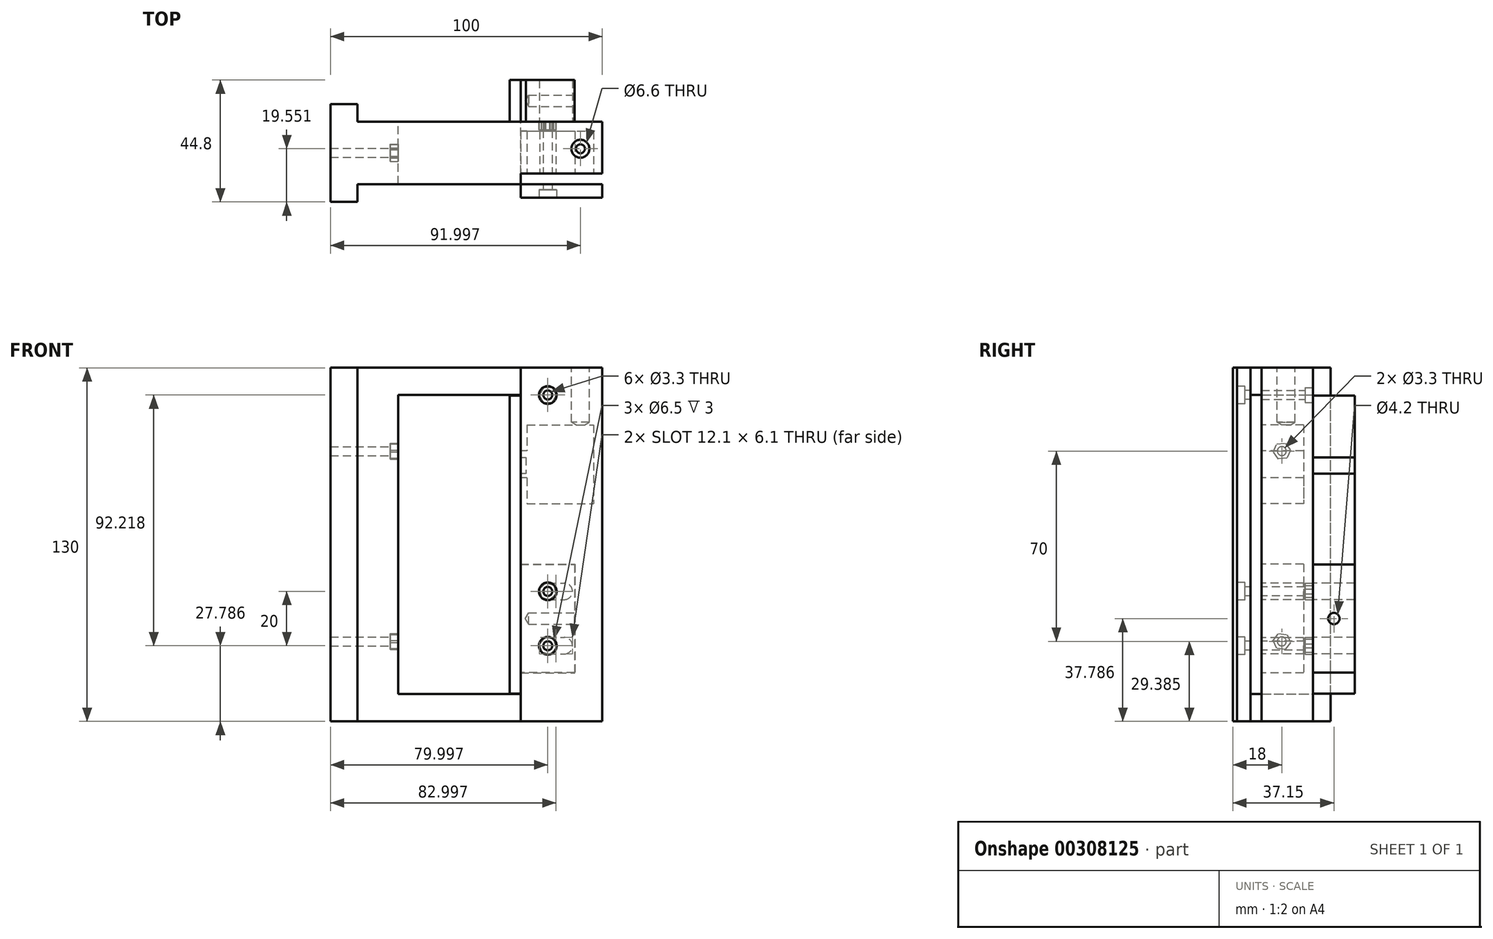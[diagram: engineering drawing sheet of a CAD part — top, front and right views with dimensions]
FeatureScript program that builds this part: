
annotation { "Feature Type Name" : "Feature", "Feature Type Description" : "" }
export const myFeature = defineFeature(function(context is Context, id is Id, definition is map)
    precondition{}
    {
        {
            var Q0;
            Q0=qCreatedBy(makeId("Front.planeOp"),FACE);
            var sketch = newSketch(context, id + "F0", { "sketchPlane" : qUnion([Q0])});
            skLineSegment(sketch, "E0", {"start": v(-34.7, 86.92) * mm, "end": v(-34.7, -43.08) * mm});
            skLineSegment(sketch, "E1", {"start": v(-34.7, -43.08) * mm, "end": v(55.3, -43.08) * mm});
            skLineSegment(sketch, "E2", {"start": v(55.3, -43.08) * mm, "end": v(55.3, 86.92) * mm});
            skLineSegment(sketch, "E3", {"start": v(55.3, 86.92) * mm, "end": v(-34.7, 86.92) * mm});
            skLineSegment(sketch, "E4.bottom", {"start": v(-19.7, 76.92) * mm, "end": v(25.3, 76.92) * mm});
            skLineSegment(sketch, "E4.top", {"start": v(-19.7, -33.08) * mm, "end": v(25.3, -33.08) * mm});
            skLineSegment(sketch, "E4.left", {"start": v(-19.7, 76.92) * mm, "end": v(-19.7, -33.08) * mm});
            skLineSegment(sketch, "E4.right", {"start": v(25.3, 76.92) * mm, "end": v(25.3, -33.08) * mm});
            skSolve(sketch);
        }
        {
            var Q0;
            Q0=makeQuery(id+"F0.imprint","IMPRINT",FACE,{"disambiguationData":[TD([[makeQuery(id+"F0.imprint","IMPRINT",EDGE,{"derivedFrom":sQuery(id+"F0.wireOp",EDGE,"E0")}),1.0]])]});
            extrude(context, id + "F1", {"entities" : qUnion([Q0]), "depth" : 23 * mm});
        }
        {
            var Q0;
            Q0=makeQuery(id+"F1.opExtrude","SWEPT_FACE",FACE,{"disambiguationData":[OSD([sQuery(id+"F0.wireOp",EDGE,"E0")])]});
            var sketch = newSketch(context, id + "F2", { "sketchPlane" : qUnion([Q0])});
            skLineSegment(sketch, "E5", {"start": v(23, 86.92) * mm, "end": v(29.5, 86.92) * mm});
            skLineSegment(sketch, "E6", {"start": v(29.5, 86.92) * mm, "end": v(29.5, -43.08) * mm});
            skLineSegment(sketch, "E7", {"start": v(29.5, -43.08) * mm, "end": v(23, -43.08) * mm});
            skLineSegment(sketch, "E8", {"start": v(23, -43.08) * mm, "end": v(0, -43.08) * mm});
            skLineSegment(sketch, "E9", {"start": v(0, -43.08) * mm, "end": v(-6.5, -43.08) * mm});
            skLineSegment(sketch, "E10", {"start": v(-6.5, -43.08) * mm, "end": v(-6.5, 86.92) * mm});
            skLineSegment(sketch, "E11", {"start": v(-6.5, 86.92) * mm, "end": v(0, 86.92) * mm});
            skSolve(sketch);
        }
        {
            var Q0;
            Q0=makeQuery(id+"F2.imprint","IMPRINT",FACE,{"disambiguationData":[TD([[makeQuery(id+"F2.imprint","IMPRINT",EDGE,{"derivedFrom":sQuery(id+"F2.wireOp",EDGE,"E9")}),-1.0]])]});
            var Q1;
            Q1=makeQuery(id+"F2.imprint","IMPRINT",FACE,{"disambiguationData":[TD([[makeQuery(id+"F2.imprint","IMPRINT",EDGE,{"derivedFrom":sQuery(id+"F2.wireOp",EDGE,"E8")}),-1.0]])]});
            var Q2;
            Q2=makeQuery(id+"F2.imprint","IMPRINT",FACE,{"disambiguationData":[TD([[makeQuery(id+"F2.imprint","IMPRINT",EDGE,{"derivedFrom":sQuery(id+"F2.wireOp",EDGE,"E5")}),-1.0]])]});
            extrude(context, id + "F3", {"entities" : qUnion([Q0, Q1, Q2]), "operationType" : NewBodyOperationType.ADD, "depth" : 10 * mm});
        }
        {
            var Q0;
            Q0=makeQuery(id+"F1.opExtrude","CAP_FACE",FACE,{"disambiguationData":[OSD([sQuery(id+"F0.wireOp",EDGE,"E0"),sQuery(id+"F0.wireOp",EDGE,"E1"),sQuery(id+"F0.wireOp",EDGE,"E2"),sQuery(id+"F0.wireOp",EDGE,"E3"),sQuery(id+"F0.wireOp",EDGE,"E4.bottom"),sQuery(id+"F0.wireOp",EDGE,"E4.top"),sQuery(id+"F0.wireOp",EDGE,"E4.left"),sQuery(id+"F0.wireOp",EDGE,"E4.right")])],"isStart":false});
            var sketch = newSketch(context, id + "F4", { "sketchPlane" : qUnion([Q0])});
            skLineSegment(sketch, "E12.bottom", {"start": v(55.3, 86.92) * mm, "end": v(25.3, 86.92) * mm});
            skLineSegment(sketch, "E12.top", {"start": v(55.3, -43.08) * mm, "end": v(25.3, -43.08) * mm});
            skLineSegment(sketch, "E12.left", {"start": v(55.3, 86.92) * mm, "end": v(55.3, -43.08) * mm});
            skLineSegment(sketch, "E12.right", {"start": v(25.3, 86.92) * mm, "end": v(25.3, -43.08) * mm});
            skSolve(sketch);
        }
        {
            var Q0;
            {var subQ2=sQuery(id+"F4.wireOp",EDGE,"E12.bottom");Q0=makeQuery(id+"F4.imprint","IMPRINT",FACE,{"disambiguationData":[TD([[makeQuery(id+"F4.imprint","IMPRINT",EDGE,{"derivedFrom":subQ2}),1.0]])]});}
            extrude(context, id + "F5", {"entities" : qUnion([Q0]), "operationType" : NewBodyOperationType.REMOVE, "oppositeDirection" : true, "depth" : 4 * mm});
        }
        {
            var Q0;
            Q0=makeQuery(id+"F5.boolean.opBoolean","COPY",FACE,{"derivedFrom":makeQuery(id+"F5.opExtrude","CAP_FACE",FACE,{"disambiguationData":[OSD([sQuery(id+"F4.wireOp",EDGE,"E12.bottom"),sQuery(id+"F4.wireOp",EDGE,"E12.top"),sQuery(id+"F4.wireOp",EDGE,"E12.left"),sQuery(id+"F4.wireOp",EDGE,"E12.right")])],"isStart":false})});
            var sketch = newSketch(context, id + "F6", { "sketchPlane" : qUnion([Q0])});
            skLineSegment(sketch, "E13.bottom", {"start": v(27.63, 65.92) * mm, "end": v(52.13, 65.92) * mm});
            skLineSegment(sketch, "E13.top", {"start": v(27.63, 36.92) * mm, "end": v(52.13, 36.92) * mm});
            skLineSegment(sketch, "E13.left", {"start": v(27.63, 65.92) * mm, "end": v(27.63, 36.92) * mm});
            skLineSegment(sketch, "E13.right", {"start": v(52.13, 65.92) * mm, "end": v(52.13, 36.92) * mm});
            skLineSegment(sketch, "E14.bottom", {"start": v(33.13, 56.42) * mm, "end": v(22.13, 56.42) * mm});
            skLineSegment(sketch, "E14.top", {"start": v(33.13, 46.42) * mm, "end": v(22.13, 46.42) * mm});
            skLineSegment(sketch, "E14.left", {"start": v(33.13, 56.42) * mm, "end": v(33.13, 46.42) * mm});
            skLineSegment(sketch, "E14.right", {"start": v(22.13, 56.42) * mm, "end": v(22.13, 46.42) * mm});
            skPoint(sketch, "E14.middle", {"position": v(27.63, 51.42) * mm});
            skLineSegment(sketch, "E15.bottom", {"start": v(52.13, 36.92) * mm, "end": v(42.13, 36.92) * mm});
            skLineSegment(sketch, "E15.top", {"start": v(52.13, 26.92) * mm, "end": v(42.13, 26.92) * mm});
            skLineSegment(sketch, "E15.left", {"start": v(52.13, 36.92) * mm, "end": v(52.13, 26.92) * mm});
            skLineSegment(sketch, "E15.right", {"start": v(42.13, 36.92) * mm, "end": v(42.13, 26.92) * mm});
            skLineSegment(sketch, "E16.bottom", {"start": v(52.13, 65.92) * mm, "end": v(42.13, 65.92) * mm});
            skLineSegment(sketch, "E16.top", {"start": v(52.13, 75.92) * mm, "end": v(42.13, 75.92) * mm});
            skLineSegment(sketch, "E16.left", {"start": v(52.13, 65.92) * mm, "end": v(52.13, 75.92) * mm});
            skLineSegment(sketch, "E16.right", {"start": v(42.13, 65.92) * mm, "end": v(42.13, 75.92) * mm});
            skLineSegment(sketch, "E17.bottom", {"start": v(25.3, 14.76) * mm, "end": v(45.3, 14.76) * mm});
            skLineSegment(sketch, "E17.top", {"start": v(25.3, -25.34) * mm, "end": v(45.3, -25.34) * mm});
            skLineSegment(sketch, "E17.left", {"start": v(25.3, 14.76) * mm, "end": v(25.3, -25.34) * mm});
            skLineSegment(sketch, "E17.right", {"start": v(45.3, 14.76) * mm, "end": v(45.3, -25.34) * mm});
            skCircle(sketch, "E18", {"center": v(35.3, 4.7) * mm, "radius": 3 * mm});
            skCircle(sketch, "E19", {"center": v(35.3, -15.3) * mm, "radius": 3 * mm});
            skLineSegment(sketch, "E20", {"start": v(45.3, -5.3) * mm, "end": v(25.3, -5.3) * mm, "construction": true});
            skSolve(sketch);
        }
        {
            var Q0;
            {var subQ4=sQuery(id+"F6.wireOp",EDGE,"E13.bottom");Q0=makeQuery(id+"F6.imprint","IMPRINT",FACE,{"disambiguationData":[TD([[makeQuery(id+"F6.imprint","IMPRINT",EDGE,{"derivedFrom":subQ4}),-1.0]])]});}
            var Q1;
            {var subQ5=sQuery(id+"F6.wireOp",EDGE,"E14.left");Q1=makeQuery(id+"F6.imprint","IMPRINT",FACE,{"disambiguationData":[TD([[makeQuery(id+"F6.imprint","IMPRINT",EDGE,{"derivedFrom":subQ5}),-1.0]])]});}
            var Q2;
            {var subQ0=sQuery(id+"F6.wireOp",EDGE,"E14.right");Q2=makeQuery(id+"F6.imprint","IMPRINT",FACE,{"disambiguationData":[TD([[makeQuery(id+"F6.imprint","IMPRINT",EDGE,{"derivedFrom":subQ0}),1.0]])]});}
            var Q3;
            {var subQ0=sQuery(id+"F6.wireOp",EDGE,"E14.bottom");var subQ1=sQuery(id+"F6.wireOp",EDGE,"E13.left");var subQ2=makeQuery(id+"F6.imprint","INTERSECT",VERTEX,{"derivedFrom":[subQ1,subQ0]});Q3=makeQuery(id+"F6.imprint","IMPRINT",FACE,{"disambiguationData":[TD([[makeQuery(id+"F6.imprint","IMPRINT",EDGE,{"disambiguationData":[TD([[subQ2,-1.0]])],"derivedFrom":subQ1}),-1.0]])]});}
            var Q4;
            Q4=makeQuery(id+"F6.imprint","IMPRINT",FACE,{"disambiguationData":[TD([[makeQuery(id+"F6.imprint","IMPRINT",EDGE,{"derivedFrom":sQuery(id+"F6.wireOp",EDGE,"E16.bottom")}),-1.0]])]});
            var Q5;
            Q5=makeQuery(id+"F6.imprint","IMPRINT",FACE,{"disambiguationData":[TD([[makeQuery(id+"F6.imprint","IMPRINT",EDGE,{"derivedFrom":sQuery(id+"F6.wireOp",EDGE,"E15.bottom")}),1.0]])]});
            var Q6;
            Q6=makeQuery(id+"F6.imprint","IMPRINT",FACE,{"disambiguationData":[TD([[makeQuery(id+"F6.imprint","IMPRINT",EDGE,{"derivedFrom":sQuery(id+"F6.wireOp",EDGE,"E17.bottom")}),-1.0]])]});
            extrude(context, id + "F7", {"entities" : qUnion([Q0, Q1, Q2, Q3, Q4, Q5, Q6]), "operationType" : NewBodyOperationType.REMOVE, "oppositeDirection" : true, "depth" : 15.5 * mm});
        }
        {
            var Q0;
            Q0=makeQuery(id+"F0.imprint","IMPRINT",FACE,{"disambiguationData":[TD([[makeQuery(id+"F0.imprint","IMPRINT",EDGE,{"derivedFrom":sQuery(id+"F0.wireOp",EDGE,"E0")}),1.0]])]});
            var sketch = newSketch(context, id + "F8", { "sketchPlane" : qUnion([Q0])});
            skPoint(sketch, "E21.0", {"position": v(35.3, -15.3) * mm});
            skLineSegment(sketch, "E22", {"start": v(35.3, -15.3) * mm, "end": v(35.3, 86.3) * mm, "construction": true});
            skPoint(sketch, "E23", {"position": v(35.3, 76.92) * mm});
            skSolve(sketch);
        }
        {
            var Q0;
            Q0=sQuery(id+"F6.wireOp",VERTEX,"E18.center");
            var Q1;
            Q1=sQuery(id+"F6.wireOp",VERTEX,"E19.center");
            var Q2;
            Q2=makeQuery(id+"F1.opExtrude","SWEPT_BODY",BODY,{"disambiguationData":[OSD([sQuery(id+"F0.wireOp",EDGE,"E0"),sQuery(id+"F0.wireOp",EDGE,"E1"),sQuery(id+"F0.wireOp",EDGE,"E2"),sQuery(id+"F0.wireOp",EDGE,"E3"),sQuery(id+"F0.wireOp",EDGE,"E4.bottom"),sQuery(id+"F0.wireOp",EDGE,"E4.top"),sQuery(id+"F0.wireOp",EDGE,"E4.left"),sQuery(id+"F0.wireOp",EDGE,"E4.right")])]});
            hole(context, id + "F9", {"style" : HoleStyle.SIMPLE, "endStyle" : HoleEndStyle.BLIND, "standardTappedOrClearance" : lookupTablePath({ "standard" : "ISO", "fit" : "Normal", "size" : "M3", "type" : "Clearance" }), "standardBlindInLast" : lookupTablePath({ "fit" : "Standard", "standard" : "ISO", "size" : "M3", "type" : "Clearance" }), "holeDiameter" : 3.3 * mm, "holeDepth" : 40 * mm, "isTappedThrough" : true, "tappedDepth" : 12 * mm, "tapClearance" : 3, "locations" : qUnion([Q0, Q1]), "scope" : qUnion([Q2])});
        }
        {
            var Q0;
            Q0=sQuery(id+"F8.wireOp",VERTEX,"E23");
            var Q1;
            Q1=makeQuery(id+"F1.opExtrude","SWEPT_BODY",BODY,{"disambiguationData":[OSD([sQuery(id+"F0.wireOp",EDGE,"E0"),sQuery(id+"F0.wireOp",EDGE,"E1"),sQuery(id+"F0.wireOp",EDGE,"E2"),sQuery(id+"F0.wireOp",EDGE,"E3"),sQuery(id+"F0.wireOp",EDGE,"E4.bottom"),sQuery(id+"F0.wireOp",EDGE,"E4.top"),sQuery(id+"F0.wireOp",EDGE,"E4.left"),sQuery(id+"F0.wireOp",EDGE,"E4.right")])]});
            hole(context, id + "F10", {"style" : HoleStyle.SIMPLE, "endStyle" : HoleEndStyle.BLIND, "oppositeDirection" : true, "standardTappedOrClearance" : lookupTablePath({ "standard" : "ISO", "fit" : "Normal", "size" : "M3", "type" : "Clearance" }), "standardBlindInLast" : lookupTablePath({ "fit" : "Standard", "standard" : "ISO", "size" : "M3", "type" : "Clearance" }), "holeDiameter" : 3.3 * mm, "holeDepth" : 40 * mm, "isTappedThrough" : true, "tappedDepth" : 12 * mm, "tapClearance" : 3, "locations" : qUnion([Q0]), "scope" : qUnion([Q1])});
        }
        {
            var Q0;
            Q0=makeQuery(id+"F1.opExtrude","SWEPT_FACE",FACE,{"disambiguationData":[OSD([sQuery(id+"F0.wireOp",EDGE,"E4.left")])]});
            var sketch = newSketch(context, id + "F11", { "sketchPlane" : qUnion([Q0])});
            skPoint(sketch, "E24", {"position": v(-11.5, 56.3) * mm});
            skPoint(sketch, "E25", {"position": v(-11.5, -13.7) * mm});
            skSolve(sketch);
        }
        {
            var Q0;
            Q0=sQuery(id+"F11.wireOp",VERTEX,"E24");
            var Q1;
            Q1=sQuery(id+"F11.wireOp",VERTEX,"E25");
            var Q2;
            Q2=makeQuery(id+"F1.opExtrude","SWEPT_BODY",BODY,{"disambiguationData":[OSD([sQuery(id+"F0.wireOp",EDGE,"E0"),sQuery(id+"F0.wireOp",EDGE,"E1"),sQuery(id+"F0.wireOp",EDGE,"E2"),sQuery(id+"F0.wireOp",EDGE,"E3"),sQuery(id+"F0.wireOp",EDGE,"E4.bottom"),sQuery(id+"F0.wireOp",EDGE,"E4.top"),sQuery(id+"F0.wireOp",EDGE,"E4.left"),sQuery(id+"F0.wireOp",EDGE,"E4.right")])]});
            hole(context, id + "F12", {"style" : HoleStyle.SIMPLE, "endStyle" : HoleEndStyle.BLIND, "standardTappedOrClearance" : lookupTablePath({ "standard" : "ISO", "fit" : "Normal", "size" : "M3", "type" : "Clearance" }), "standardBlindInLast" : lookupTablePath({ "fit" : "Standard", "standard" : "ISO", "size" : "M3", "type" : "Clearance" }), "holeDiameter" : 3.3 * mm, "holeDepth" : 40 * mm, "isTappedThrough" : true, "tappedDepth" : 12 * mm, "tapClearance" : 3, "locations" : qUnion([Q0, Q1]), "scope" : qUnion([Q2])});
        }
        {
            var Q0;
            Q0=qCreatedBy(makeId("Front.planeOp"),FACE);
            var sketch = newSketch(context, id + "F13", { "sketchPlane" : qUnion([Q0])});
            skPoint(sketch, "E26.0", {"position": v(25.3, 14.76) * mm});
            skPoint(sketch, "E27.0", {"position": v(25.3, -25.34) * mm});
            skPoint(sketch, "E28.0", {"position": v(25.3, -33.08) * mm});
            skLineSegment(sketch, "E29", {"start": v(25.3, 76.72) * mm, "end": v(25.3, 54.02) * mm});
            skLineSegment(sketch, "E30", {"start": v(25.3, -25.14) * mm, "end": v(25.3, -32.88) * mm});
            skLineSegment(sketch, "E31", {"start": v(21.3, 76.72) * mm, "end": v(21.3, 48.02) * mm});
            skPoint(sketch, "E32.0", {"position": v(35.3, 4.7) * mm});
            skPoint(sketch, "E33.0", {"position": v(35.3, -15.3) * mm});
            skPoint(sketch, "E34", {"position": v(41.3, 4.7) * mm});
            skPoint(sketch, "E35", {"position": v(41.3, -15.3) * mm});
            skCircle(sketch, "E36", {"center": v(41.3, 4.7) * mm, "radius": 3.05 * mm});
            skCircle(sketch, "E37", {"center": v(41.3, -15.3) * mm, "radius": 3.05 * mm});
            skCircle(sketch, "E38", {"center": v(35.3, -15.3) * mm, "radius": 3.05 * mm});
            skCircle(sketch, "E39", {"center": v(35.3, 4.7) * mm, "radius": 3.05 * mm});
            skLineSegment(sketch, "E40", {"start": v(35.3, 7.76) * mm, "end": v(35.3, -18.34) * mm, "construction": true});
            skLineSegment(sketch, "E41", {"start": v(41.3, 7.76) * mm, "end": v(41.3, -18.34) * mm, "construction": true});
            skLineSegment(sketch, "E42", {"start": v(35.3, 7.76) * mm, "end": v(41.3, 7.76) * mm});
            skLineSegment(sketch, "E43", {"start": v(35.3, -18.34) * mm, "end": v(41.3, -18.34) * mm});
            skLineSegment(sketch, "E44", {"start": v(35.3, 1.66) * mm, "end": v(41.3, 1.66) * mm});
            skLineSegment(sketch, "E45", {"start": v(35.3, -12.24) * mm, "end": v(41.3, -12.24) * mm});
            skLineSegment(sketch, "E46.1", {"start": v(45.2, 14.56) * mm, "end": v(45.2, -25.14) * mm});
            skLineSegment(sketch, "E47.0", {"start": v(25.3, 76.72) * mm, "end": v(21.3, 76.72) * mm});
            skLineSegment(sketch, "E48.0", {"start": v(25.3, -32.88) * mm, "end": v(21.3, -32.88) * mm});
            skLineSegment(sketch, "E49.0", {"start": v(45.2, -25.14) * mm, "end": v(25.3, -25.14) * mm});
            skLineSegment(sketch, "E50.0", {"start": v(25.3, 14.56) * mm, "end": v(45.2, 14.56) * mm});
            skLineSegment(sketch, "E51.trimOffspring", {"start": v(21.3, 48.02) * mm, "end": v(21.3, -32.88) * mm});
            skLineSegment(sketch, "E52", {"start": v(25.3, 54.02) * mm, "end": v(27.3, 54.02) * mm});
            skLineSegment(sketch, "E53", {"start": v(27.3, 54.02) * mm, "end": v(27.3, 48.02) * mm});
            skLineSegment(sketch, "E54", {"start": v(27.3, 48.02) * mm, "end": v(25.3, 48.02) * mm});
            skPoint(sketch, "E55.orphan", {"position": v(21.3, 54.02) * mm});
            skLineSegment(sketch, "E56.trimOffspring", {"start": v(25.3, 48.02) * mm, "end": v(25.3, 14.56) * mm});
            skSolve(sketch);
        }
        {
            var Q0;
            Q0=makeQuery(id+"F13.imprint","IMPRINT",FACE,{"disambiguationData":[TD([[makeQuery(id+"F13.imprint","IMPRINT",EDGE,{"derivedFrom":sQuery(id+"F13.wireOp",EDGE,"E29")}),-1.0]])]});
            extrude(context, id + "F14", {"entities" : qUnion([Q0]), "oppositeDirection" : true, "depth" : 15.3 * mm});
        }
        {
            var Q0;
            {var subQ2=sQuery(id+"F4.wireOp",EDGE,"E12.bottom");Q0=makeQuery(id+"F4.imprint","IMPRINT",FACE,{"disambiguationData":[TD([[makeQuery(id+"F4.imprint","IMPRINT",EDGE,{"derivedFrom":subQ2}),1.0]])]});}
            extrude(context, id + "F15", {"entities" : qUnion([Q0]), "depth" : 5 * mm});
        }
        {
            var Q0;
            Q0=makeQuery(id+"F15.opExtrude","CAP_FACE",FACE,{"disambiguationData":[OSD([sQuery(id+"F4.wireOp",EDGE,"E12.bottom"),sQuery(id+"F4.wireOp",EDGE,"E12.top"),sQuery(id+"F4.wireOp",EDGE,"E12.left"),sQuery(id+"F4.wireOp",EDGE,"E12.right")])],"isStart":false});
            var sketch = newSketch(context, id + "F16", { "sketchPlane" : qUnion([Q0])});
            skPoint(sketch, "E57.0", {"position": v(35.3, -15.3) * mm});
            skPoint(sketch, "E58.0", {"position": v(35.3, 4.7) * mm});
            skPoint(sketch, "E59.0", {"position": v(35.3, 76.92) * mm});
            skSolve(sketch);
        }
        {
            var Q0;
            Q0=sQuery(id+"F16.wireOp",VERTEX,"E59.0");
            var Q1;
            Q1=sQuery(id+"F16.wireOp",VERTEX,"E58.0");
            var Q2;
            Q2=sQuery(id+"F16.wireOp",VERTEX,"E57.0");
            var Q3;
            Q3=makeQuery(id+"F15.opExtrude","SWEPT_BODY",BODY,{"disambiguationData":[OSD([sQuery(id+"F4.wireOp",EDGE,"E12.bottom"),sQuery(id+"F4.wireOp",EDGE,"E12.top"),sQuery(id+"F4.wireOp",EDGE,"E12.left"),sQuery(id+"F4.wireOp",EDGE,"E12.right")])]});
            hole(context, id + "F17", {"style" : HoleStyle.C_BORE, "endStyle" : HoleEndStyle.BLIND, "standardTappedOrClearance" : lookupTablePath({ "standard" : "ISO", "fit" : "Normal", "size" : "M3", "type" : "Clearance" }), "standardBlindInLast" : lookupTablePath({ "fit" : "Standard", "standard" : "ISO", "size" : "M3", "type" : "Clearance" }), "holeDiameter" : 3.3 * mm, "cBoreDiameter" : 6.5 * mm, "cBoreDepth" : 3 * mm, "holeDepth" : 40 * mm, "isTappedThrough" : true, "tappedDepth" : 12 * mm, "tapClearance" : 3, "locations" : qUnion([Q0, Q1, Q2]), "scope" : qUnion([Q3])});
        }
        {
            var Q0;
            {var subQ0=sQuery(id+"F0.wireOp",EDGE,"E3");Q0=makeQuery(id+"F3.boolean.opBoolean","MERGE",FACE,{"derivedFrom":[makeQuery(id+"F1.opExtrude","SWEPT_FACE",FACE,{"disambiguationData":[OSD([subQ0])]}),makeQuery(id+"F3.opExtrude","SWEPT_FACE",FACE,{"disambiguationData":[OSD([sQuery(id+"F0.wireOp",EDGE,"E0"),subQ0,sQuery(id+"F2.wireOp",EDGE,"E5"),sQuery(id+"F2.wireOp",EDGE,"E11")])]})]});}
            var sketch = newSketch(context, id + "F18", { "sketchPlane" : qUnion([Q0])});
            skPoint(sketch, "E60", {"position": v(47.3, -9.95) * mm});
            skPoint(sketch, "E61", {"position": v(44.13, -9.95) * mm});
            skSolve(sketch);
        }
        {
            var Q0;
            Q0=sQuery(id+"F18.wireOp",VERTEX,"E60");
            var Q1;
            Q1=makeQuery(id+"F1.opExtrude","SWEPT_BODY",BODY,{"disambiguationData":[OSD([sQuery(id+"F0.wireOp",EDGE,"E0"),sQuery(id+"F0.wireOp",EDGE,"E1"),sQuery(id+"F0.wireOp",EDGE,"E2"),sQuery(id+"F0.wireOp",EDGE,"E3"),sQuery(id+"F0.wireOp",EDGE,"E4.bottom"),sQuery(id+"F0.wireOp",EDGE,"E4.top"),sQuery(id+"F0.wireOp",EDGE,"E4.left"),sQuery(id+"F0.wireOp",EDGE,"E4.right")])]});
            hole(context, id + "F19", {"style" : HoleStyle.SIMPLE, "endStyle" : HoleEndStyle.BLIND, "standardTappedOrClearance" : lookupTablePath({ "standard" : "ISO", "fit" : "Normal", "size" : "M6", "type" : "Clearance" }), "standardBlindInLast" : lookupTablePath({ "fit" : "Standard", "standard" : "ISO", "size" : "M6", "type" : "Clearance" }), "holeDiameter" : 6.6 * mm, "holeDepth" : 20 * mm, "isTappedThrough" : true, "tappedDepth" : 12 * mm, "tapClearance" : 3, "locations" : qUnion([Q0]), "scope" : qUnion([Q1])});
        }
        {
            var Q0;
            Q0=makeQuery(id+"F1.opExtrude","CAP_FACE",FACE,{"disambiguationData":[OSD([sQuery(id+"F0.wireOp",EDGE,"E0"),sQuery(id+"F0.wireOp",EDGE,"E1"),sQuery(id+"F0.wireOp",EDGE,"E2"),sQuery(id+"F0.wireOp",EDGE,"E3"),sQuery(id+"F0.wireOp",EDGE,"E4.bottom"),sQuery(id+"F0.wireOp",EDGE,"E4.top"),sQuery(id+"F0.wireOp",EDGE,"E4.left"),sQuery(id+"F0.wireOp",EDGE,"E4.right")])],"isStart":true});
            var sketch = newSketch(context, id + "F20", { "sketchPlane" : qUnion([Q0])});
            skCircle(sketch, "E62.cCircle", {"center": v(-35.3, 76.92) * mm, "radius": 2.75 * mm, "construction": true});
            skLineSegment(sketch, "E62.0", {"start": v(-33.7, 74.17) * mm, "end": v(-36.88, 74.17) * mm});
            skLineSegment(sketch, "E62.1", {"start": v(-36.88, 74.17) * mm, "end": v(-38.47, 76.92) * mm});
            skLineSegment(sketch, "E62.2", {"start": v(-38.47, 76.92) * mm, "end": v(-36.88, 79.67) * mm});
            skLineSegment(sketch, "E62.3", {"start": v(-36.88, 79.67) * mm, "end": v(-33.7, 79.67) * mm});
            skLineSegment(sketch, "E62.4", {"start": v(-33.7, 79.67) * mm, "end": v(-32.12, 76.92) * mm});
            skLineSegment(sketch, "E62.5", {"start": v(-32.12, 76.92) * mm, "end": v(-33.7, 74.17) * mm});
            skPoint(sketch, "E62.0.midPoint", {"position": v(-35.3, 74.17) * mm});
            skCircle(sketch, "E63.cCircle", {"center": v(-35.3, 4.7) * mm, "radius": 2.75 * mm, "construction": true});
            skLineSegment(sketch, "E63.0", {"start": v(-34.55, 7.8) * mm, "end": v(-32.25, 5.6) * mm});
            skLineSegment(sketch, "E63.1", {"start": v(-32.25, 5.6) * mm, "end": v(-33, 2.51) * mm});
            skLineSegment(sketch, "E63.2", {"start": v(-33, 2.51) * mm, "end": v(-36.05, 1.62) * mm});
            skLineSegment(sketch, "E63.3", {"start": v(-36.05, 1.62) * mm, "end": v(-38.34, 3.81) * mm});
            skLineSegment(sketch, "E63.4", {"start": v(-38.34, 3.81) * mm, "end": v(-37.6, 6.9) * mm});
            skLineSegment(sketch, "E63.5", {"start": v(-37.6, 6.9) * mm, "end": v(-34.55, 7.8) * mm});
            skPoint(sketch, "E63.0.midPoint", {"position": v(-33.4, 6.7) * mm});
            skCircle(sketch, "E64.cCircle", {"center": v(-35.3, -15.3) * mm, "radius": 2.8 * mm, "construction": true});
            skLineSegment(sketch, "E64.0", {"start": v(-34.28, -12.21) * mm, "end": v(-32.12, -14.64) * mm});
            skLineSegment(sketch, "E64.1", {"start": v(-32.12, -14.64) * mm, "end": v(-33.14, -17.71) * mm});
            skLineSegment(sketch, "E64.2", {"start": v(-33.14, -17.71) * mm, "end": v(-36.31, -18.37) * mm});
            skLineSegment(sketch, "E64.3", {"start": v(-36.31, -18.37) * mm, "end": v(-38.47, -15.95) * mm});
            skLineSegment(sketch, "E64.4", {"start": v(-38.47, -15.95) * mm, "end": v(-37.45, -12.87) * mm});
            skLineSegment(sketch, "E64.5", {"start": v(-37.45, -12.87) * mm, "end": v(-34.28, -12.21) * mm});
            skPoint(sketch, "E64.0.midPoint", {"position": v(-33.2, -13.42) * mm});
            skSolve(sketch);
        }
        {
            var Q0;
            Q0=makeQuery(id+"F20.imprint","IMPRINT",FACE,{"disambiguationData":[TD([[makeQuery(id+"F20.imprint","IMPRINT",EDGE,{"derivedFrom":sQuery(id+"F20.wireOp",EDGE,"E63.0")}),-1.0]])]});
            var Q1;
            Q1=makeQuery(id+"F20.imprint","IMPRINT",FACE,{"disambiguationData":[TD([[makeQuery(id+"F20.imprint","IMPRINT",EDGE,{"derivedFrom":sQuery(id+"F20.wireOp",EDGE,"E64.0")}),-1.0]])]});
            var Q2;
            Q2=makeQuery(id+"F20.imprint","IMPRINT",FACE,{"disambiguationData":[TD([[makeQuery(id+"F20.imprint","IMPRINT",EDGE,{"derivedFrom":sQuery(id+"F20.wireOp",EDGE,"E62.0")}),-1.0]])]});
            extrude(context, id + "F21", {"entities" : qUnion([Q0, Q1, Q2]), "operationType" : NewBodyOperationType.REMOVE, "oppositeDirection" : true, "depth" : 3 * mm});
        }
        {
            var Q0;
            Q0=makeQuery(id+"F1.opExtrude","SWEPT_FACE",FACE,{"disambiguationData":[OSD([sQuery(id+"F0.wireOp",EDGE,"E4.left")])]});
            var sketch = newSketch(context, id + "F22", { "sketchPlane" : qUnion([Q0])});
            skCircle(sketch, "E65.cCircle", {"center": v(-11.5, 56.3) * mm, "radius": 2.77 * mm, "construction": true});
            skLineSegment(sketch, "E65.0", {"start": v(-8.32, 56.64) * mm, "end": v(-9.62, 53.72) * mm});
            skLineSegment(sketch, "E65.1", {"start": v(-9.62, 53.72) * mm, "end": v(-12.8, 53.39) * mm});
            skLineSegment(sketch, "E65.2", {"start": v(-12.8, 53.39) * mm, "end": v(-14.68, 55.97) * mm});
            skLineSegment(sketch, "E65.3", {"start": v(-14.68, 55.97) * mm, "end": v(-13.38, 58.89) * mm});
            skLineSegment(sketch, "E65.4", {"start": v(-13.38, 58.89) * mm, "end": v(-10.2, 59.22) * mm});
            skLineSegment(sketch, "E65.5", {"start": v(-10.2, 59.22) * mm, "end": v(-8.32, 56.64) * mm});
            skPoint(sketch, "E65.0.midPoint", {"position": v(-8.97, 55.18) * mm});
            skCircle(sketch, "E66.cCircle", {"center": v(-11.5, -13.7) * mm, "radius": 2.75 * mm, "construction": true});
            skLineSegment(sketch, "E66.0", {"start": v(-9.6, -11.15) * mm, "end": v(-8.35, -14.07) * mm});
            skLineSegment(sketch, "E66.1", {"start": v(-8.35, -14.07) * mm, "end": v(-10.25, -16.61) * mm});
            skLineSegment(sketch, "E66.2", {"start": v(-10.25, -16.61) * mm, "end": v(-13.4, -16.24) * mm});
            skLineSegment(sketch, "E66.3", {"start": v(-13.4, -16.24) * mm, "end": v(-14.65, -13.32) * mm});
            skLineSegment(sketch, "E66.4", {"start": v(-14.65, -13.32) * mm, "end": v(-12.75, -10.78) * mm});
            skLineSegment(sketch, "E66.5", {"start": v(-12.75, -10.78) * mm, "end": v(-9.6, -11.15) * mm});
            skPoint(sketch, "E66.0.midPoint", {"position": v(-8.97, -12.6) * mm});
            skSolve(sketch);
        }
        {
            var Q0;
            Q0=makeQuery(id+"F22.imprint","IMPRINT",FACE,{"disambiguationData":[TD([[makeQuery(id+"F22.imprint","IMPRINT",EDGE,{"derivedFrom":sQuery(id+"F22.wireOp",EDGE,"E65.0")}),-1.0]])]});
            var Q1;
            Q1=makeQuery(id+"F22.imprint","IMPRINT",FACE,{"disambiguationData":[TD([[makeQuery(id+"F22.imprint","IMPRINT",EDGE,{"derivedFrom":sQuery(id+"F22.wireOp",EDGE,"E66.0")}),-1.0]])]});
            extrude(context, id + "F23", {"entities" : qUnion([Q0, Q1]), "operationType" : NewBodyOperationType.REMOVE, "oppositeDirection" : true, "depth" : 3 * mm});
        }
        {
            var Q0;
            Q0=makeQuery(id+"F14.opExtrude","SWEPT_FACE",FACE,{"disambiguationData":[OSD([sQuery(id+"F13.wireOp",EDGE,"E46.1")])]});
            var sketch = newSketch(context, id + "F24", { "sketchPlane" : qUnion([Q0])});
            skPoint(sketch, "E67.positionSnap0", {"position": v(0, -5.3) * mm});
            skLineSegment(sketch, "E68", {"start": v(15.3, -5.3) * mm, "end": v(0, -5.3) * mm, "construction": true});
            skLineSegment(sketch, "E69", {"start": v(7.65, 14.56) * mm, "end": v(7.65, -25.14) * mm, "construction": true});
            skPoint(sketch, "E70", {"position": v(7.65, -5.3) * mm});
            skSolve(sketch);
        }
        {
            var Q0;
            Q0=sQuery(id+"F24.wireOp",VERTEX,"E70");
            var Q1;
            Q1=makeQuery(id+"F14.opExtrude","SWEPT_BODY",BODY,{"disambiguationData":[OSD([sQuery(id+"F13.wireOp",EDGE,"E29"),sQuery(id+"F13.wireOp",EDGE,"E30"),sQuery(id+"F13.wireOp",EDGE,"E31"),sQuery(id+"F13.wireOp",EDGE,"E36"),sQuery(id+"F13.wireOp",EDGE,"E37"),sQuery(id+"F13.wireOp",EDGE,"E38"),sQuery(id+"F13.wireOp",EDGE,"E39"),sQuery(id+"F13.wireOp",EDGE,"E42"),sQuery(id+"F13.wireOp",EDGE,"E43"),sQuery(id+"F13.wireOp",EDGE,"E44"),sQuery(id+"F13.wireOp",EDGE,"E45"),sQuery(id+"F13.wireOp",EDGE,"E46.1"),sQuery(id+"F13.wireOp",EDGE,"E47.0"),sQuery(id+"F13.wireOp",EDGE,"E48.0"),sQuery(id+"F13.wireOp",EDGE,"E49.0"),sQuery(id+"F13.wireOp",EDGE,"E50.0"),sQuery(id+"F13.wireOp",EDGE,"E51.trimOffspring"),sQuery(id+"F13.wireOp",EDGE,"E52"),sQuery(id+"F13.wireOp",EDGE,"E53"),sQuery(id+"F13.wireOp",EDGE,"E54"),sQuery(id+"F13.wireOp",EDGE,"E56.trimOffspring")])]});
            hole(context, id + "F25", {"style" : HoleStyle.SIMPLE, "endStyle" : HoleEndStyle.BLIND, "standardTappedOrClearance" : lookupTablePath({ "standard" : "ISO", "fit" : "Close", "size" : "M4", "type" : "Clearance" }), "standardBlindInLast" : lookupTablePath({ "fit" : "Close", "standard" : "ISO", "size" : "M4", "type" : "Clearance" }), "holeDiameter" : 4.2 * mm, "holeDepth" : 17 * mm, "isTappedThrough" : true, "tappedDepth" : 12 * mm, "tapClearance" : 3, "locations" : qUnion([Q0]), "scope" : qUnion([Q1])});
        }
    });
